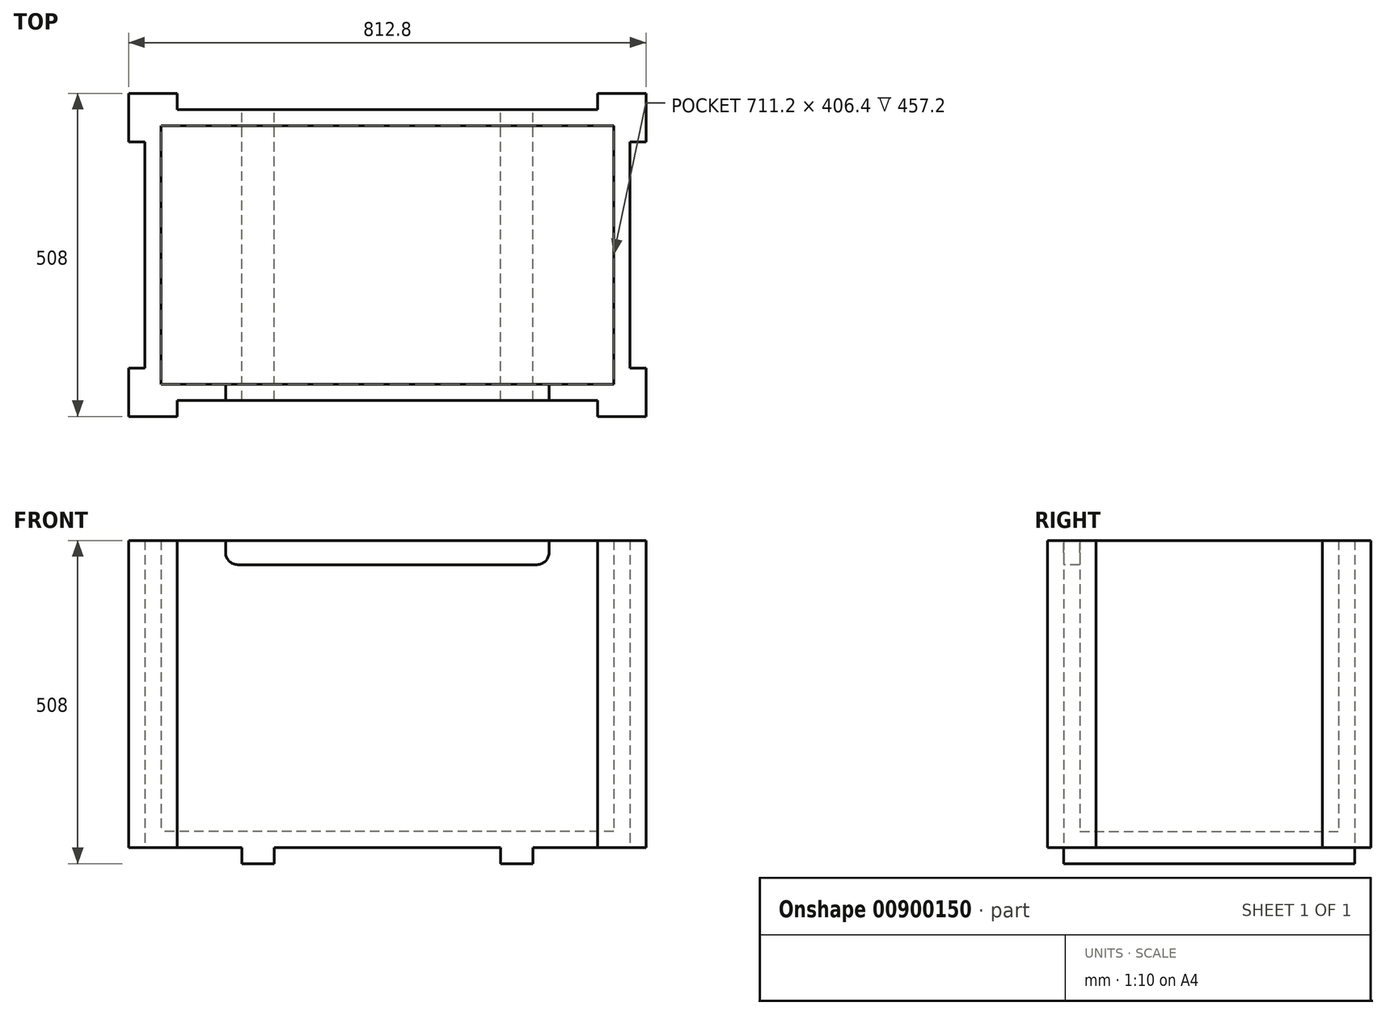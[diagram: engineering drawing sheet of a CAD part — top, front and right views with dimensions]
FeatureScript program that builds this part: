
annotation { "Feature Type Name" : "Feature", "Feature Type Description" : "" }
export const myFeature = defineFeature(function(context is Context, id is Id, definition is map)
    precondition{}
    {
        {
            var Q0;
            Q0=qCreatedBy(makeId("Top.planeOp"),FACE);
            var sketch = newSketch(context, id + "F0", { "sketchPlane" : qUnion([Q0])});
            skLineSegment(sketch, "E0.bottom", {"start": v(0, 0) * mm, "end": v(-762, 0) * mm});
            skLineSegment(sketch, "E0.top", {"start": v(0, 457.2) * mm, "end": v(-762, 457.2) * mm});
            skLineSegment(sketch, "E0.left", {"start": v(0, 0) * mm, "end": v(0, 457.2) * mm});
            skLineSegment(sketch, "E0.right", {"start": v(-762, 0) * mm, "end": v(-762, 457.2) * mm});
            skSolve(sketch);
        }
        {
            var Q0;
            Q0=makeQuery(id+"F0.imprint","IMPRINT",FACE,{"disambiguationData":[TD([[makeQuery(id+"F0.imprint","IMPRINT",EDGE,{"derivedFrom":sQuery(id+"F0.wireOp",EDGE,"E0.bottom")}),-1.0]])]});
            extrude(context, id + "F1", {"entities" : qUnion([Q0]), "depth" : 25.4 * mm, "offsetDistance" : 25.4 * mm});
        }
        {
            var Q0;
            Q0=makeQuery(id+"F1.opExtrude","CAP_FACE",FACE,{"disambiguationData":[OSD([sQuery(id+"F0.wireOp",EDGE,"E0.bottom"),sQuery(id+"F0.wireOp",EDGE,"E0.top"),sQuery(id+"F0.wireOp",EDGE,"E0.left"),sQuery(id+"F0.wireOp",EDGE,"E0.right")])],"isStart":true});
            var sketch = newSketch(context, id + "F2", { "sketchPlane" : qUnion([Q0])});
            skLineSegment(sketch, "E1.bottom", {"start": v(-609.6, 0) * mm, "end": v(-558.8, 0) * mm});
            skLineSegment(sketch, "E1.top", {"start": v(-609.6, -457.2) * mm, "end": v(-558.8, -457.2) * mm});
            skLineSegment(sketch, "E1.left", {"start": v(-609.6, 0) * mm, "end": v(-609.6, -457.2) * mm});
            skLineSegment(sketch, "E1.right", {"start": v(-558.8, 0) * mm, "end": v(-558.8, -457.2) * mm});
            skLineSegment(sketch, "E2.bottom", {"start": v(-203.2, 0) * mm, "end": v(-152.4, 0) * mm});
            skLineSegment(sketch, "E2.top", {"start": v(-203.2, -457.2) * mm, "end": v(-152.4, -457.2) * mm});
            skLineSegment(sketch, "E2.left", {"start": v(-203.2, 0) * mm, "end": v(-203.2, -457.2) * mm});
            skLineSegment(sketch, "E2.right", {"start": v(-152.4, 0) * mm, "end": v(-152.4, -457.2) * mm});
            skSolve(sketch);
        }
        {
            var Q0;
            Q0=makeQuery(id+"F2.imprint","IMPRINT",FACE,{"disambiguationData":[TD([[makeQuery(id+"F2.imprint","IMPRINT",EDGE,{"derivedFrom":sQuery(id+"F2.wireOp",EDGE,"E1.bottom")}),1.0]])]});
            var Q1;
            Q1=makeQuery(id+"F2.imprint","IMPRINT",FACE,{"disambiguationData":[TD([[makeQuery(id+"F2.imprint","IMPRINT",EDGE,{"derivedFrom":sQuery(id+"F2.wireOp",EDGE,"E2.bottom")}),1.0]])]});
            extrude(context, id + "F3", {"entities" : qUnion([Q0, Q1]), "operationType" : NewBodyOperationType.ADD, "depth" : 25.4 * mm, "offsetDistance" : 25.4 * mm});
        }
        {
            var Q0;
            Q0=makeQuery(id+"F1.opExtrude","CAP_FACE",FACE,{"disambiguationData":[OSD([sQuery(id+"F0.wireOp",EDGE,"E0.bottom"),sQuery(id+"F0.wireOp",EDGE,"E0.top"),sQuery(id+"F0.wireOp",EDGE,"E0.left"),sQuery(id+"F0.wireOp",EDGE,"E0.right")])],"isStart":false});
            var sketch = newSketch(context, id + "F4", { "sketchPlane" : qUnion([Q0])});
            skLineSegment(sketch, "E3", {"start": v(0, 457.2) * mm, "end": v(-762, 457.2) * mm});
            skLineSegment(sketch, "E4", {"start": v(-762, 457.2) * mm, "end": v(-762, 0) * mm});
            skLineSegment(sketch, "E5", {"start": v(-762, 0) * mm, "end": v(0, 0) * mm});
            skLineSegment(sketch, "E6", {"start": v(0, 0) * mm, "end": v(0, 457.2) * mm});
            skLineSegment(sketch, "E7.bottom", {"start": v(-25.4, 25.4) * mm, "end": v(-736.6, 25.4) * mm});
            skLineSegment(sketch, "E7.top", {"start": v(-25.4, 431.8) * mm, "end": v(-736.6, 431.8) * mm});
            skLineSegment(sketch, "E7.left", {"start": v(-25.4, 25.4) * mm, "end": v(-25.4, 431.8) * mm});
            skLineSegment(sketch, "E7.right", {"start": v(-736.6, 25.4) * mm, "end": v(-736.6, 431.8) * mm});
            skSolve(sketch);
        }
        {
            var Q0;
            Q0 = qSketchRegion(id + "F4", true);
            extrude(context, id + "F5", {"entities" : qUnion([Q0]), "operationType" : NewBodyOperationType.ADD, "depth" : 457.2 * mm, "offsetDistance" : 25.4 * mm});
        }
        {
            var Q0;
            Q0=makeQuery(id+"F5.boolean.opBoolean","MERGE",FACE,{"derivedFrom":[makeQuery(id+"F3.boolean.opBoolean","MERGE",FACE,{"derivedFrom":[makeQuery(id+"F1.opExtrude","SWEPT_FACE",FACE,{"disambiguationData":[OSD([sQuery(id+"F0.wireOp",EDGE,"E0.top")])]}),makeQuery(id+"F3.opExtrude","SWEPT_FACE",FACE,{"disambiguationData":[OSD([sQuery(id+"F2.wireOp",EDGE,"E1.top")])]}),makeQuery(id+"F3.opExtrude","SWEPT_FACE",FACE,{"disambiguationData":[OSD([sQuery(id+"F2.wireOp",EDGE,"E2.top")])]})]}),makeQuery(id+"F5.opExtrude","SWEPT_FACE",FACE,{"disambiguationData":[OSD([sQuery(id+"F4.wireOp",EDGE,"E3")])]})]});
            var sketch = newSketch(context, id + "F6", { "sketchPlane" : qUnion([Q0])});
            skLineSegment(sketch, "E8.bottom", {"start": v(0, 482.6) * mm, "end": v(50.8, 482.6) * mm});
            skLineSegment(sketch, "E8.top", {"start": v(0, 0) * mm, "end": v(50.8, 0) * mm});
            skLineSegment(sketch, "E8.left", {"start": v(0, 482.6) * mm, "end": v(0, 0) * mm});
            skLineSegment(sketch, "E8.right", {"start": v(50.8, 482.6) * mm, "end": v(50.8, 0) * mm});
            skLineSegment(sketch, "E9.bottom", {"start": v(762, 482.6) * mm, "end": v(711.2, 482.6) * mm});
            skLineSegment(sketch, "E9.top", {"start": v(762, 0) * mm, "end": v(711.2, 0) * mm});
            skLineSegment(sketch, "E9.left", {"start": v(762, 482.6) * mm, "end": v(762, 0) * mm});
            skLineSegment(sketch, "E9.right", {"start": v(711.2, 482.6) * mm, "end": v(711.2, 0) * mm});
            skSolve(sketch);
        }
        {
            var Q0;
            Q0 = qSketchRegion(id + "F6", true);
            extrude(context, id + "F7", {"entities" : qUnion([Q0]), "operationType" : NewBodyOperationType.ADD, "depth" : 25.4 * mm, "offsetDistance" : 25.4 * mm});
        }
        {
            var Q0;
            Q0=makeQuery(id+"F5.boolean.opBoolean","MERGE",FACE,{"derivedFrom":[makeQuery(id+"F3.boolean.opBoolean","MERGE",FACE,{"derivedFrom":[makeQuery(id+"F1.opExtrude","SWEPT_FACE",FACE,{"disambiguationData":[OSD([sQuery(id+"F0.wireOp",EDGE,"E0.bottom")])]}),makeQuery(id+"F3.opExtrude","SWEPT_FACE",FACE,{"disambiguationData":[OSD([sQuery(id+"F2.wireOp",EDGE,"E1.bottom")])]}),makeQuery(id+"F3.opExtrude","SWEPT_FACE",FACE,{"disambiguationData":[OSD([sQuery(id+"F2.wireOp",EDGE,"E2.bottom")])]})]}),makeQuery(id+"F5.opExtrude","SWEPT_FACE",FACE,{"disambiguationData":[OSD([sQuery(id+"F4.wireOp",EDGE,"E5")])]})]});
            var sketch = newSketch(context, id + "F8", { "sketchPlane" : qUnion([Q0])});
            skLineSegment(sketch, "E10.bottom", {"start": v(-762, 482.6) * mm, "end": v(-711.2, 482.6) * mm});
            skLineSegment(sketch, "E10.top", {"start": v(-762, 0) * mm, "end": v(-711.2, 0) * mm});
            skLineSegment(sketch, "E10.left", {"start": v(-762, 482.6) * mm, "end": v(-762, 0) * mm});
            skLineSegment(sketch, "E10.right", {"start": v(-711.2, 482.6) * mm, "end": v(-711.2, 0) * mm});
            skLineSegment(sketch, "E11.bottom", {"start": v(0, 482.6) * mm, "end": v(-50.8, 482.6) * mm});
            skLineSegment(sketch, "E11.top", {"start": v(0, 0) * mm, "end": v(-50.8, 0) * mm});
            skLineSegment(sketch, "E11.left", {"start": v(0, 482.6) * mm, "end": v(0, 0) * mm});
            skLineSegment(sketch, "E11.right", {"start": v(-50.8, 482.6) * mm, "end": v(-50.8, 0) * mm});
            skSolve(sketch);
        }
        {
            var Q0;
            Q0 = qSketchRegion(id + "F8", true);
            extrude(context, id + "F9", {"entities" : qUnion([Q0]), "operationType" : NewBodyOperationType.ADD, "depth" : 25.4 * mm, "offsetDistance" : 25.4 * mm});
        }
        {
            var Q0;
            Q0=makeQuery(id+"F9.boolean.opBoolean","MERGE",FACE,{"derivedFrom":[makeQuery(id+"F7.boolean.opBoolean","MERGE",FACE,{"derivedFrom":[makeQuery(id+"F5.boolean.opBoolean","MERGE",FACE,{"derivedFrom":[makeQuery(id+"F1.opExtrude","SWEPT_FACE",FACE,{"disambiguationData":[OSD([sQuery(id+"F0.wireOp",EDGE,"E0.left")])]}),makeQuery(id+"F5.opExtrude","SWEPT_FACE",FACE,{"disambiguationData":[OSD([sQuery(id+"F4.wireOp",EDGE,"E6")])]})]}),makeQuery(id+"F7.opExtrude","SWEPT_FACE",FACE,{"disambiguationData":[OSD([sQuery(id+"F6.wireOp",EDGE,"E8.left")])]})]}),makeQuery(id+"F9.opExtrude","SWEPT_FACE",FACE,{"disambiguationData":[OSD([sQuery(id+"F8.wireOp",EDGE,"E11.left")])]})]});
            var sketch = newSketch(context, id + "F10", { "sketchPlane" : qUnion([Q0])});
            skLineSegment(sketch, "E12.bottom", {"start": v(-25.4, 482.6) * mm, "end": v(50.8, 482.6) * mm});
            skLineSegment(sketch, "E12.top", {"start": v(-25.4, 0) * mm, "end": v(50.8, 0) * mm});
            skLineSegment(sketch, "E12.left", {"start": v(-25.4, 482.6) * mm, "end": v(-25.4, 0) * mm});
            skLineSegment(sketch, "E12.right", {"start": v(50.8, 482.6) * mm, "end": v(50.8, 0) * mm});
            skLineSegment(sketch, "E13.bottom", {"start": v(482.6, 482.6) * mm, "end": v(406.4, 482.6) * mm});
            skLineSegment(sketch, "E13.top", {"start": v(482.6, 0) * mm, "end": v(406.4, 0) * mm});
            skLineSegment(sketch, "E13.left", {"start": v(482.6, 482.6) * mm, "end": v(482.6, 0) * mm});
            skLineSegment(sketch, "E13.right", {"start": v(406.4, 482.6) * mm, "end": v(406.4, 0) * mm});
            skSolve(sketch);
        }
        {
            var Q0;
            Q0 = qSketchRegion(id + "F10", true);
            extrude(context, id + "F11", {"entities" : qUnion([Q0]), "operationType" : NewBodyOperationType.ADD, "depth" : 25.4 * mm, "offsetDistance" : 25.4 * mm});
        }
        {
            var Q0;
            Q0=makeQuery(id+"F9.boolean.opBoolean","MERGE",FACE,{"derivedFrom":[makeQuery(id+"F7.boolean.opBoolean","MERGE",FACE,{"derivedFrom":[makeQuery(id+"F5.boolean.opBoolean","MERGE",FACE,{"derivedFrom":[makeQuery(id+"F1.opExtrude","SWEPT_FACE",FACE,{"disambiguationData":[OSD([sQuery(id+"F0.wireOp",EDGE,"E0.right")])]}),makeQuery(id+"F5.opExtrude","SWEPT_FACE",FACE,{"disambiguationData":[OSD([sQuery(id+"F4.wireOp",EDGE,"E4")])]})]}),makeQuery(id+"F7.opExtrude","SWEPT_FACE",FACE,{"disambiguationData":[OSD([sQuery(id+"F6.wireOp",EDGE,"E9.left")])]})]}),makeQuery(id+"F9.opExtrude","SWEPT_FACE",FACE,{"disambiguationData":[OSD([sQuery(id+"F8.wireOp",EDGE,"E10.left")])]})]});
            var sketch = newSketch(context, id + "F12", { "sketchPlane" : qUnion([Q0])});
            skLineSegment(sketch, "E14.bottom", {"start": v(-482.6, 482.6) * mm, "end": v(-406.4, 482.6) * mm});
            skLineSegment(sketch, "E14.top", {"start": v(-482.6, 0) * mm, "end": v(-406.4, 0) * mm});
            skLineSegment(sketch, "E14.left", {"start": v(-482.6, 482.6) * mm, "end": v(-482.6, 0) * mm});
            skLineSegment(sketch, "E14.right", {"start": v(-406.4, 482.6) * mm, "end": v(-406.4, 0) * mm});
            skLineSegment(sketch, "E15.bottom", {"start": v(25.4, 482.6) * mm, "end": v(-50.8, 482.6) * mm});
            skLineSegment(sketch, "E15.top", {"start": v(25.4, 0) * mm, "end": v(-50.8, 0) * mm});
            skLineSegment(sketch, "E15.left", {"start": v(25.4, 482.6) * mm, "end": v(25.4, 0) * mm});
            skLineSegment(sketch, "E15.right", {"start": v(-50.8, 482.6) * mm, "end": v(-50.8, 0) * mm});
            skSolve(sketch);
        }
        {
            var Q0;
            Q0 = qSketchRegion(id + "F12", true);
            extrude(context, id + "F13", {"entities" : qUnion([Q0]), "operationType" : NewBodyOperationType.ADD, "depth" : 25.4 * mm, "offsetDistance" : 25.4 * mm});
        }
        {
            var Q0;
            Q0=makeQuery(id+"F5.boolean.opBoolean","MERGE",FACE,{"derivedFrom":[makeQuery(id+"F3.boolean.opBoolean","MERGE",FACE,{"derivedFrom":[makeQuery(id+"F1.opExtrude","SWEPT_FACE",FACE,{"disambiguationData":[OSD([sQuery(id+"F0.wireOp",EDGE,"E0.bottom")])]}),makeQuery(id+"F3.opExtrude","SWEPT_FACE",FACE,{"disambiguationData":[OSD([sQuery(id+"F2.wireOp",EDGE,"E1.bottom")])]}),makeQuery(id+"F3.opExtrude","SWEPT_FACE",FACE,{"disambiguationData":[OSD([sQuery(id+"F2.wireOp",EDGE,"E2.bottom")])]})]}),makeQuery(id+"F5.opExtrude","SWEPT_FACE",FACE,{"disambiguationData":[OSD([sQuery(id+"F4.wireOp",EDGE,"E5")])]})]});
            var sketch = newSketch(context, id + "F14", { "sketchPlane" : qUnion([Q0])});
            skArc(sketch, "E16", {"start": v(-635, 463.55) * mm, "mid": v(-629.42, 450.08) * mm, "end": v(-615.95, 444.5) * mm});
            skArc(sketch, "E17", {"start": v(-146.05, 444.5) * mm, "mid": v(-132.58, 450.08) * mm, "end": v(-127, 463.55) * mm});
            skLineSegment(sketch, "E18", {"start": v(-615.95, 444.5) * mm, "end": v(-146.05, 444.5) * mm});
            skLineSegment(sketch, "E19", {"start": v(-127, 463.55) * mm, "end": v(-127, 482.6) * mm});
            skLineSegment(sketch, "E20", {"start": v(-635, 463.55) * mm, "end": v(-635, 482.6) * mm});
            skLineSegment(sketch, "E21", {"start": v(-635, 482.6) * mm, "end": v(-127, 482.6) * mm});
            skSolve(sketch);
        }
        {
            var Q0;
            Q0=makeQuery(id+"F14.imprint","IMPRINT",FACE,{"disambiguationData":[TD([[makeQuery(id+"F14.imprint","IMPRINT",EDGE,{"derivedFrom":sQuery(id+"F14.wireOp",EDGE,"E16")}),1.0]])]});
            extrude(context, id + "F15", {"entities" : qUnion([Q0]), "operationType" : NewBodyOperationType.REMOVE, "oppositeDirection" : true, "depth" : 25.4 * mm, "offsetDistance" : 25.4 * mm});
        }
    });
